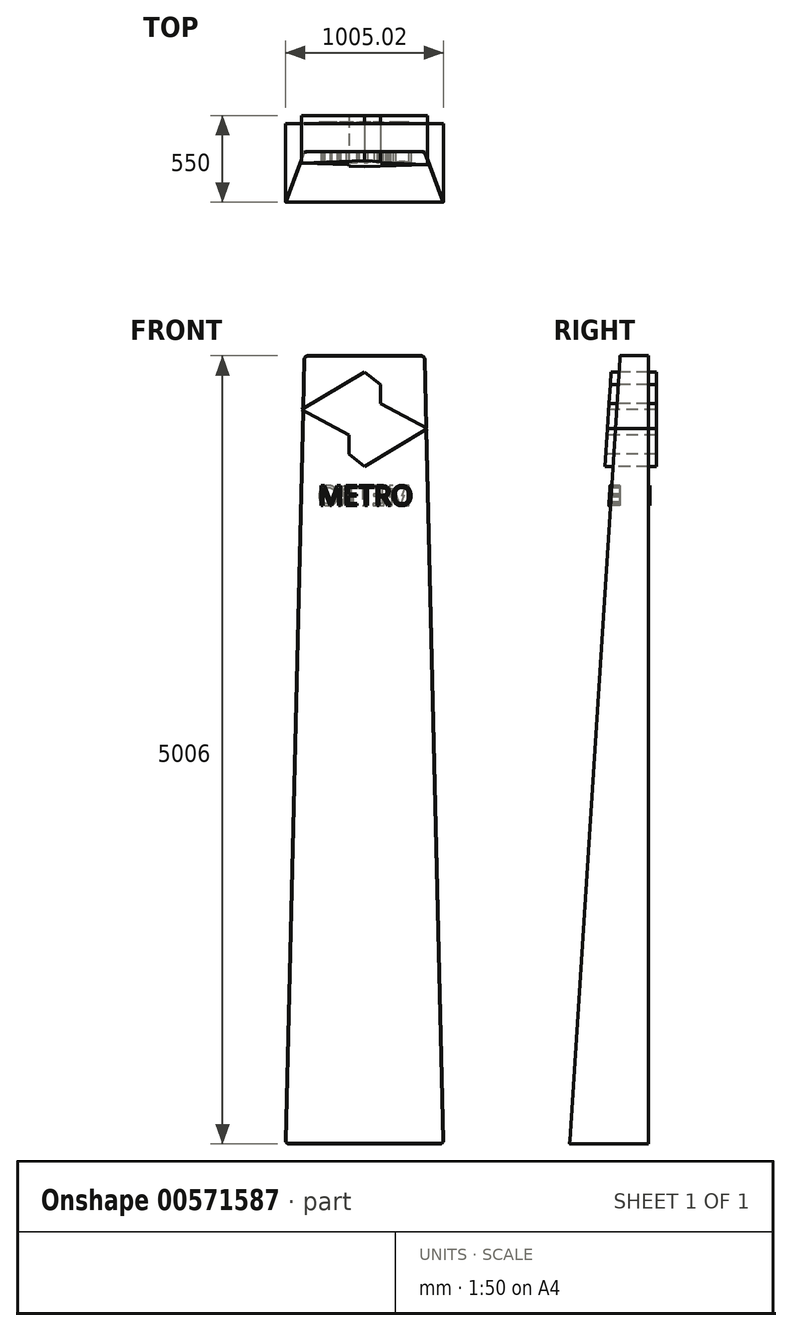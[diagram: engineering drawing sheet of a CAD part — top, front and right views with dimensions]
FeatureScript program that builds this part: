
annotation { "Feature Type Name" : "Feature", "Feature Type Description" : "" }
export const myFeature = defineFeature(function(context is Context, id is Id, definition is map)
    precondition{}
    {
        {
            var Q0;
            Q0=qCreatedBy(makeId("Front.planeOp"),FACE);
            var sketch = newSketch(context, id + "F0", { "sketchPlane" : qUnion([Q0])});
            skLineSegment(sketch, "E0.bottom", {"start": v(-500, 2500) * mm, "end": v(500, 2500) * mm});
            skLineSegment(sketch, "E0.top", {"start": v(-500, -2500) * mm, "end": v(500, -2500) * mm});
            skLineSegment(sketch, "E0.left", {"start": v(-500, 2500) * mm, "end": v(-500, -2500) * mm, "construction": true});
            skLineSegment(sketch, "E0.right", {"start": v(500, 2500) * mm, "end": v(500, -2500) * mm, "construction": true});
            skLineSegment(sketch, "E1", {"start": v(0, -2500) * mm, "end": v(0, 2500) * mm, "construction": true});
            skLineSegment(sketch, "E2", {"start": v(-500, -2500) * mm, "end": v(-380, 2500) * mm});
            skLineSegment(sketch, "E3.MirrorCS", {"start": v(500, -2500) * mm, "end": v(380, 2500) * mm});
            skSolve(sketch);
        }
        {
            var Q0;
            Q0=qSketchRegion(id+"F0",true);
            extrude(context, id + "F1", {"entities" : qUnion([Q0]), "depth" : 500 * mm, "offsetDistance" : 25 * mm, "symmetric" : true});
        }
        {
            var Q0;
            Q0=qCreatedBy(makeId("Right.planeOp"),FACE);
            var sketch = newSketch(context, id + "F2", { "sketchPlane" : qUnion([Q0])});
            skLineSegment(sketch, "E4.0", {"start": v(-250, -2500) * mm, "end": v(-250, 2500) * mm});
            skLineSegment(sketch, "E5", {"start": v(-250, -2500) * mm, "end": v(87.37, 2771.45) * mm});
            skLineSegment(sketch, "E6.0", {"start": v(-250, 2500) * mm, "end": v(250, 2500) * mm, "construction": true});
            skLineSegment(sketch, "E7", {"start": v(87.37, 2771.45) * mm, "end": v(-250, 2771.45) * mm});
            skLineSegment(sketch, "E8", {"start": v(-250, 2771.45) * mm, "end": v(-250, 2500) * mm});
            skPoint(sketch, "E9", {"position": v(70, 2500) * mm});
            skSolve(sketch);
        }
        {
            var Q0;
            Q0=qSketchRegion(id+"F2",true);
            extrude(context, id + "F3", {"entities" : qUnion([Q0]), "operationType" : NewBodyOperationType.REMOVE, "oppositeDirection" : true, "depth" : 2000 * mm, "offsetDistance" : 25 * mm, "symmetric" : true});
        }
        {
            var Q0;
            Q0=makeQuery(id+"F1.opExtrude","SWEPT_EDGE",EDGE,{"disambiguationData":[OSD([sQuery(id+"F0.wireOp",EDGE,"E0.bottom"),sQuery(id+"F0.wireOp",EDGE,"E0.left")])]});
            var Q1;
            Q1=makeQuery(id+"F1.opExtrude","SWEPT_EDGE",EDGE,{"disambiguationData":[OSD([sQuery(id+"F0.wireOp",EDGE,"E0.bottom"),sQuery(id+"F0.wireOp",EDGE,"E0.right")])]});
            var Q2;
            Q2=makeQuery(id+"F1.opExtrude","SWEPT_EDGE",EDGE,{"disambiguationData":[OSD([sQuery(id+"F0.wireOp",EDGE,"E0.top"),sQuery(id+"F0.wireOp",EDGE,"E0.left")])]});
            var Q3;
            Q3=makeQuery(id+"F1.opExtrude","SWEPT_EDGE",EDGE,{"disambiguationData":[OSD([sQuery(id+"F0.wireOp",EDGE,"E0.top"),sQuery(id+"F0.wireOp",EDGE,"E0.right")])]});
            fillet(context, id + "F4", {"entities" : qUnion([Q0, Q1, Q2, Q3]), "radius" : 20 * mm, "tangentPropagation" : true, "allowEdgeOverflow" : false});
        }
        {
            var Q0;
            Q0=qCreatedBy(makeId("Front.planeOp"),FACE);
            var sketch = newSketch(context, id + "F5", { "sketchPlane" : qUnion([Q0])});
            skLineSegment(sketch, "E10.0.0", {"start": v(-479.51, -2500) * mm, "end": v(479.51, -2500) * mm});
            skArc(sketch, "E10.0.1", {"start": v(479.51, -2500) * mm, "mid": v(493.83, -2493.97) * mm, "end": v(499.5, -2479.52) * mm});
            skLineSegment(sketch, "E10.0.2", {"start": v(499.5, -2479.52) * mm, "end": v(380.47, 2480.48) * mm});
            skArc(sketch, "E10.0.3", {"start": v(380.47, 2480.48) * mm, "mid": v(374.45, 2494.31) * mm, "end": v(360.47, 2500) * mm});
            skLineSegment(sketch, "E10.0.4", {"start": v(360.47, 2500) * mm, "end": v(-360.47, 2500) * mm});
            skArc(sketch, "E10.0.5", {"start": v(-360.47, 2500) * mm, "mid": v(-374.45, 2494.31) * mm, "end": v(-380.47, 2480.48) * mm});
            skLineSegment(sketch, "E10.0.6", {"start": v(-380.47, 2480.48) * mm, "end": v(-499.5, -2479.52) * mm});
            skArc(sketch, "E10.0.7", {"start": v(-499.5, -2479.52) * mm, "mid": v(-493.83, -2493.97) * mm, "end": v(-479.51, -2500) * mm});
            skArc(sketch, "E11.0", {"start": v(479.51, -2503) * mm, "mid": v(495.97, -2496.07) * mm, "end": v(502.5, -2479.45) * mm});
            skLineSegment(sketch, "E11.1", {"start": v(-479.51, -2503) * mm, "end": v(479.51, -2503) * mm});
            skLineSegment(sketch, "E11.2", {"start": v(502.5, -2479.45) * mm, "end": v(383.47, 2480.55) * mm});
            skArc(sketch, "E11.3", {"start": v(-502.5, -2479.45) * mm, "mid": v(-495.97, -2496.07) * mm, "end": v(-479.51, -2503) * mm});
            skArc(sketch, "E11.4", {"start": v(383.47, 2480.55) * mm, "mid": v(376.54, 2496.46) * mm, "end": v(360.47, 2503) * mm});
            skLineSegment(sketch, "E11.5", {"start": v(360.47, 2503) * mm, "end": v(-360.47, 2503) * mm});
            skArc(sketch, "E11.6", {"start": v(-360.47, 2503) * mm, "mid": v(-376.54, 2496.46) * mm, "end": v(-383.47, 2480.55) * mm});
            skLineSegment(sketch, "E11.7", {"start": v(-383.47, 2480.55) * mm, "end": v(-502.5, -2479.45) * mm});
            skSolve(sketch);
        }
        {
            var Q0;
            Q0=qSketchRegion(id+"F5",true);
            extrude(context, id + "F6", {"entities" : qUnion([Q0]), "depth" : 500 * mm, "offsetDistance" : 25 * mm, "symmetric" : true});
        }
        {
            var Q0;
            Q0=qCreatedBy(makeId("Front.planeOp"),FACE);
            cPlane(context, id + "F7", {"entities" : qUnion([Q0]), "cplaneType" : CPlaneType.OFFSET, "offset" : 730 * mm, "width" : 150 * mm, "height" : 150 * mm});
        }
        {
            var Q0;
            Q0=qSketchRegion(id+"F2",true);
            extrude(context, id + "F8", {"entities" : qUnion([Q0]), "operationType" : NewBodyOperationType.REMOVE, "oppositeDirection" : true, "depth" : 5000 * mm, "offsetDistance" : 25 * mm, "symmetric" : true});
        }
        {
            var Q0;
            Q0=qCreatedBy(id+"F7.planeOp",FACE);
            var sketch = newSketch(context, id + "F9", { "sketchPlane" : qUnion([Q0])});
            skLineSegment(sketch, "E12", {"start": v(0, 0) * mm, "end": v(0, 2768.76) * mm, "construction": true});
            skLineSegment(sketch, "E13.0", {"start": v(-479.83, 2500) * mm, "end": v(480, 2500) * mm, "construction": true});
            skLineSegment(sketch, "E14", {"start": v(-400, 2100) * mm, "end": v(400, 2100) * mm, "construction": true});
            skLineSegment(sketch, "E15", {"start": v(-400, 2400) * mm, "end": v(-400, 1800) * mm, "construction": true});
            skLineSegment(sketch, "E16", {"start": v(-400, 2400) * mm, "end": v(400, 2400) * mm, "construction": true});
            skLineSegment(sketch, "E17", {"start": v(400, 2400) * mm, "end": v(400, 1800) * mm, "construction": true});
            skLineSegment(sketch, "E18", {"start": v(400, 1800) * mm, "end": v(-400, 1800) * mm, "construction": true});
            skLineSegment(sketch, "E19", {"start": v(-120, 1800) * mm, "end": v(-120, 2400) * mm, "construction": true});
            skLineSegment(sketch, "E20", {"start": v(120, 2400) * mm, "end": v(120, 1800) * mm, "construction": true});
            skLineSegment(sketch, "E21", {"start": v(-400, 2160) * mm, "end": v(400, 2160) * mm, "construction": true});
            skLineSegment(sketch, "E22", {"start": v(-400, 2040) * mm, "end": v(400, 2040) * mm, "construction": true});
            skPoint(sketch, "E23", {"position": v(0, 2400) * mm});
            skLineSegment(sketch, "E24", {"start": v(100, 2320) * mm, "end": v(100, 2200) * mm});
            skLineSegment(sketch, "E25", {"start": v(100, 2200) * mm, "end": v(400, 2040) * mm});
            skLineSegment(sketch, "E26", {"start": v(-100, 1880) * mm, "end": v(-100, 2000) * mm});
            skLineSegment(sketch, "E27", {"start": v(-100, 2000) * mm, "end": v(-400, 2160) * mm});
            skLineSegment(sketch, "E28", {"start": v(-100, 1880) * mm, "end": v(0, 1800) * mm});
            skLineSegment(sketch, "E29", {"start": v(0, 1800) * mm, "end": v(400, 2040) * mm});
            skLineSegment(sketch, "E30", {"start": v(100, 2320) * mm, "end": v(0, 2400) * mm});
            skLineSegment(sketch, "E31", {"start": v(-400, 2160) * mm, "end": v(0, 2400) * mm});
            skSolve(sketch);
        }
        {
            var Q0;
            Q0=qSketchRegion(id+"F9",true);
            extrude(context, id + "F10", {"entities" : qUnion([Q0]), "oppositeDirection" : true, "depth" : 1200 * mm, "hasOffset" : true, "offsetDistance" : 100 * mm});
        }
        {
            var Q0;
            Q0=qCreatedBy(makeId("Right.planeOp"),FACE);
            var sketch = newSketch(context, id + "F11", { "sketchPlane" : qUnion([Q0])});
            skLineSegment(sketch, "E32.0", {"start": v(300, 2480.92) * mm, "end": v(300, -2479.08) * mm});
            skLineSegment(sketch, "E33.0", {"start": v(-298.56, -2475.89) * mm, "end": v(18.88, 2484.11) * mm});
            skLineSegment(sketch, "E34", {"start": v(300, 2480.92) * mm, "end": v(814.8, 2480.92) * mm});
            skLineSegment(sketch, "E35", {"start": v(814.8, 2480.92) * mm, "end": v(628.56, -2172.37) * mm});
            skLineSegment(sketch, "E36", {"start": v(628.56, -2172.37) * mm, "end": v(300, -2479.08) * mm});
            skLineSegment(sketch, "E37", {"start": v(-298.56, -2475.89) * mm, "end": v(-1431.88, 2639.66) * mm});
            skLineSegment(sketch, "E38", {"start": v(-1431.88, 2639.66) * mm, "end": v(18.88, 2484.11) * mm});
            skSolve(sketch);
        }
        {
            var Q0;
            Q0=qSketchRegion(id+"F11",true);
            extrude(context, id + "F12", {"entities" : qUnion([Q0]), "operationType" : NewBodyOperationType.REMOVE, "oppositeDirection" : true, "depth" : 2000 * mm, "offsetDistance" : 25 * mm, "symmetric" : true});
        }
        {
            var Q0;
            Q0=qCreatedBy(id+"F7.planeOp",FACE);
            var sketch = newSketch(context, id + "F13", { "sketchPlane" : qUnion([Q0])});
            skText(sketch, "E39", { "text": "METRO", "fontName": "OpenSans-Regular.ttf"});
            const initialGuessF13  = {"E39": [-0.29324, 1.55181, 1, 0, 0.12658]};
            skSetInitialGuess(sketch, initialGuessF13);
            skSolve(sketch);
        }
        {
            var Q0;
            Q0=qSketchRegion(id+"F13",true);
            var Q1;
            Q1=makeQuery(id+"F3.boolean.opBoolean","COPY",FACE,{"derivedFrom":makeQuery(id+"F3.opExtrude","SWEPT_FACE",FACE,{"disambiguationData":[OSD([sQuery(id+"F2.wireOp",EDGE,"ZJW6kHRR-rWZL-W2R4-lTON-FJxPeIBoXaOv")])]})});
            extrude(context, id + "F14", {"entities" : qUnion([Q0]), "oppositeDirection" : true, "depth" : 800 * mm, "endBoundEntityFace" : qUnion([Q1]), "offsetDistance" : 25 * mm});
        }
        {
            var Q0;
            Q0=qCreatedBy(makeId("Right.planeOp"),FACE);
            var sketch = newSketch(context, id + "F15", { "sketchPlane" : qUnion([Q0])});
            skLineSegment(sketch, "E40", {"start": v(9.37, 1709.17) * mm, "end": v(-869.9, 1736.78) * mm});
            skLineSegment(sketch, "E41", {"start": v(-869.9, 1736.78) * mm, "end": v(-869.9, 1416.62) * mm});
            skLineSegment(sketch, "E42", {"start": v(-869.9, 1416.62) * mm, "end": v(-9.36, 1416.62) * mm});
            skLineSegment(sketch, "E43.0", {"start": v(-9.36, 1416.62) * mm, "end": v(9.37, 1709.17) * mm});
            skSolve(sketch);
        }
        {
            var Q0;
            Q0=qSketchRegion(id+"F15",true);
            extrude(context, id + "F16", {"entities" : qUnion([Q0]), "operationType" : NewBodyOperationType.REMOVE, "oppositeDirection" : true, "depth" : 2000 * mm, "offsetDistance" : 25 * mm, "symmetric" : true});
        }
        {
            var Q0;
            Q0=makeQuery(id+"F1.opExtrude","CAP_FACE",FACE,{"disambiguationData":[OSD([sQuery(id+"F0.wireOp",EDGE,"E0.bottom"),sQuery(id+"F0.wireOp",EDGE,"E0.top"),sQuery(id+"F0.wireOp",EDGE,"E2"),sQuery(id+"F0.wireOp",EDGE,"E3.MirrorCS")])],"isStart":true});
            var sketch = newSketch(context, id + "F17", { "sketchPlane" : qUnion([Q0])});
            skText(sketch, "E44", { "text": "METRO\n", "fontName": "OpenSans-Regular.ttf"});
            skLineSegment(sketch, "E45.0", {"start": v(-12.35, 1551.81) * mm, "end": v(2.24, 1551.81) * mm, "construction": true});
            const initialGuessF17  = {"E44": [-0.3, 1.55177, 1, 0, 0.12658]};
            skSetInitialGuess(sketch, initialGuessF17);
            skSolve(sketch);
        }
        {
            var Q0;
            Q0 = qSketchRegion(id + "F17", true);
            extrude(context, id + "F18", {"entities" : qUnion([Q0]), "operationType" : NewBodyOperationType.ADD, "depth" : 10 * mm, "offsetDistance" : 25 * mm});
        }
    });
